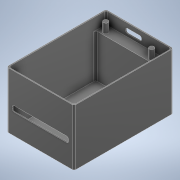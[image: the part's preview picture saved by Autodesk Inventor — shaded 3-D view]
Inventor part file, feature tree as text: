
AUTODESK INVENTOR PART (.ipt)
format: ipt  version: 2021 (Build 250183000, 183)  size: 210,944 bytes
history: native  units: mm
features: extrude x8, sketch x8, fillet x3, other x2
ambient origin geometry x8: Origin, YZ Plane, XZ Plane, XY Plane, X Axis, Y Axis, Z Axis, Center Point
bodies: Body1 (feature_tree)
feature tree (21):
  other  "Sólido1"
  extrude  "Extrusão1"  Depth=53.0mm
  extrude  "Extrusão2"  Depth=0.5mm
  extrude  "Extrusão3"  Depth=11.0mm
  fillet  "Arredondamento1"  Radius=19.5mm
  extrude  "Extrusão4"  Depth=2.5mm
  extrude  "Extrusão5"  Depth=1.0mm
  extrude  "Extrusão6"  Depth=31.5mm
  extrude  "Extrusão7"  Depth=23.0mm
  extrude  "Extrusão8"  Depth=2.5mm
  fillet  "Arredondamento3"  Radius=2.5mm
  fillet  "Arredondamento4"  Radius=24.5mm
  sketch  "Esboço1"  dims[d0=100.0mm d1=53.0mm]
  sketch  "Esboço2"  dims[d2=30.0mm d3=0.0mm d4=0.5mm]
  other  "Contorno projetado1"
  sketch  "Esboço3"  dims[d5=29.5mm d6=0.0mm d7=11.0mm d8=19.5mm]
  sketch  "Esboço4"  dims[d9=2.5mm d10=2.5mm]
  sketch  "Esboço5"  dims[d11=4.5mm d12=0.0mm d13=1.0mm]
  sketch  "Esboço6"  dims[d15=5.5mm d16=31.5mm]
  sketch  "Esboço7"  dims[d17=23.0mm d18=0.0mm d19=3.421mm]
  sketch  "Esboço8"  dims[d20=3.5mm d21=2.5mm d22=2.5mm d23=24.5mm d24=5.0mm d25=0.0mm d26=11.0mm d27=14.0mm d28=30.0mm d29=3.0mm d30=5.0mm d31=0.0mm d32=3.0mm d33=5.0mm d34=0.0mm d35=0.5mm d36=5.0mm d37=0.0mm d38=1.0mm d39=1.0mm]
